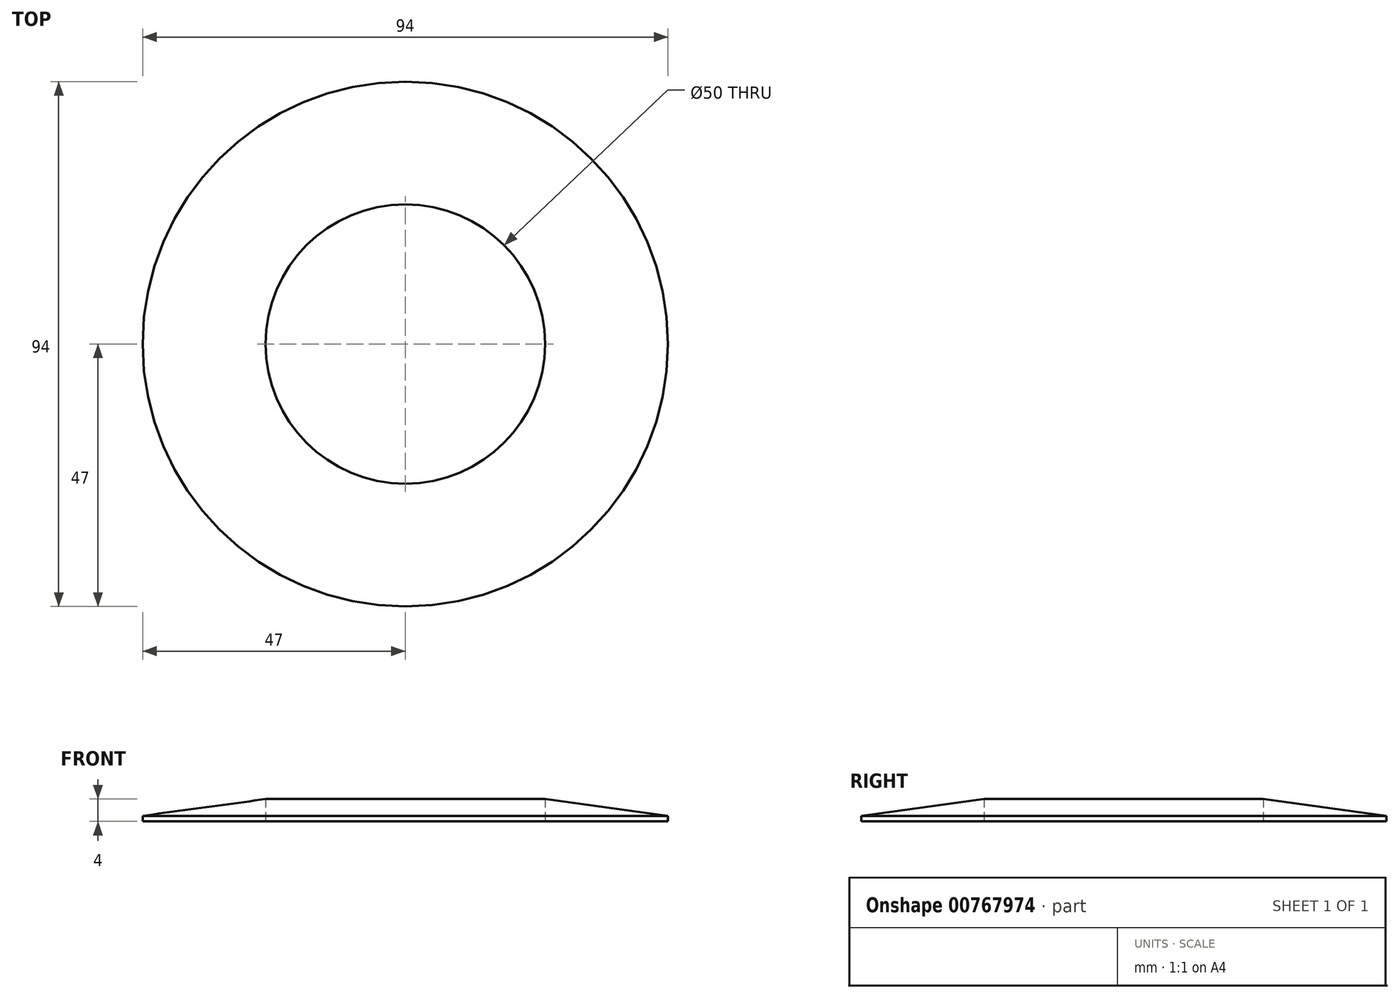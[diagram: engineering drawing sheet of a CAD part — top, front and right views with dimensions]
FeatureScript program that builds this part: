
annotation { "Feature Type Name" : "Feature", "Feature Type Description" : "" }
export const myFeature = defineFeature(function(context is Context, id is Id, definition is map)
    precondition{}
    {
        {
            var Q0;
            Q0=qCreatedBy(makeId("Front.planeOp"),FACE);
            var sketch = newSketch(context, id + "F0", { "sketchPlane" : qUnion([Q0])});
            skLineSegment(sketch, "E0", {"start": v(-25, 0) * mm, "end": v(-47, 0) * mm});
            skLineSegment(sketch, "E1", {"start": v(-47, 0) * mm, "end": v(-47, 1) * mm});
            skLineSegment(sketch, "E2", {"start": v(-25, 0) * mm, "end": v(-25, 4) * mm});
            skLineSegment(sketch, "E3", {"start": v(-25, 4) * mm, "end": v(-47, 1) * mm});
            skLineSegment(sketch, "E4", {"start": v(0, 0) * mm, "end": v(0, 4) * mm});
            skSolve(sketch);
        }
        {
            var Q0;
            Q0 = qSketchRegion(id + "F0", true);
            var Q1;
            Q1=sQuery(id+"F0.wireOp",EDGE,"E4");
            revolve(context, id + "F1", {"surfaceOperationType" : NewSurfaceOperationType.NEW, "entities" : qUnion([Q0]), "axis" : qUnion([Q1]), "revolveType" : RevolveType.FULL});
        }
    });
